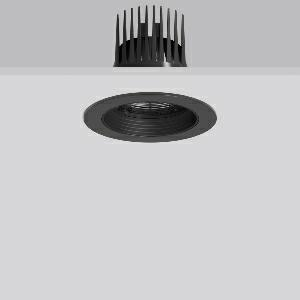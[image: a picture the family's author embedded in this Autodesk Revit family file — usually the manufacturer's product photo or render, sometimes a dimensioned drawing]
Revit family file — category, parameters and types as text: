
# Revit family: heledon_maxi_e_901790_003_2_5095
name_source: partatom
category: Lighting Fixtures
units: mm (PartAtom-declared; Revit-internal decimal feet)

## family parameters
Cut with Voids When Loaded = No
Host = Face
Light Source = No
Part Type = Normal
Room Calculation Point = No
Round Connector Dimension = Use Diameter
Shared = No

## types (1)
- HELEDON maxi E (1 x LED Modul 927 bakery, 2900 lm, 2700)
    Apparent Load = 33 VA
    Approval mark = CE
    CIE Flux Codes = 96 99 100 100 100
    Color Rendering = 90
    Color Temperature = 2700
    Default Elevation = 1800 mm
    Description = Series: HELEDON maxi
Round recessed downlight. Housing: die-cast aluminium, powder-coated. Black plastic ring and recessed LED to prevent glare from the side. Optical assembly with lens made of plastic (polycarbonate) for the best homogeneous light distribution - can be changed without tools. Special LED for illumination of pastries included. Suitable for Recessed ceiling mounting. Installation without tools thanks to spring fastening system. Including separate LED converter with connecting cable 600 mm.High quality converter without flickering and stroboscopic effect. Through-wiring box (5 pole) available as accessory. The following accessories can be mounted without use of tools: interchangeable lenses, decorative glasses, honeycomb louvre, clear and frosted diffusers, white interchangeable plastic ring. 
Colour: deep black, matt (RAL 9005)
Diameter: 162 mm
Height: 3 mm
Cut-out diameter: 152 mm
Recess height: 200 mm
Luminaire: recess height: 135 mm
Lamp: LED
Socket: without socket
Colour temperature: bakery
Colour rendering index (CRI): 97
System power: 33 W
Rated luminous flux: 2900 lm
Luminous efficiency: 88 lm/W
Control gear: Regulated power supply
Protection class: II
Type of protection: IP 20
    Height = 0 mm  [stored 0 ft]
    Lamp = 1 x LED Modul 927 bakery
    Lamp Light Flux = 2900 lm
    Lamp count = 1
    Length = 162 mm
    Lifetime = 50000 h
    Luminous efficacy = 88 lm/W
    Manufacturer = RZB
    ModVariant = No
    Model = 901790.003.2
    Mounting Place = Ceiling
    Mounting Type = Recessed
    Number of Poles = 1
    OnlyDefault = Yes
    Power Factor = 1
    Product Name = HELEDON maxi E
    Product group = Recessed downlights
    ProductGroupID = 402
    Protection Class = Protection class II
    Protection Degree = IP 20
    RLX_Detail_Level = 1
    RLX_Emergency_Light_Flux = 0 lm
    RLX_Emergency_Type = 0
    RLX_Emergency_Type_DB = No
    RlxData = <blob elided: 124497 chars, md5=bee06f6c>
    Socket = socket
    Standby Power = 0 W
    System Light Flux = 2900 lm
    System Power = 33 W
    Type Comments = Product without accessories
    Type Image = 901663.003.jpg
    URL = http://relux.com
    VarID = ---
    Voltage = 230 V
    Voltage Range = 220-240 V
    Weight = 0.00 kg
    Width = 0 mm  [stored 0 ft]

note: [stored X ft] marks values corroborated as IEEE doubles in the binary element streams (Revit-internal decimal feet)

## geometry (parser evidence)
native form markers: Blend x4, Sweep x12
no freeform markers — native parametric forms only
